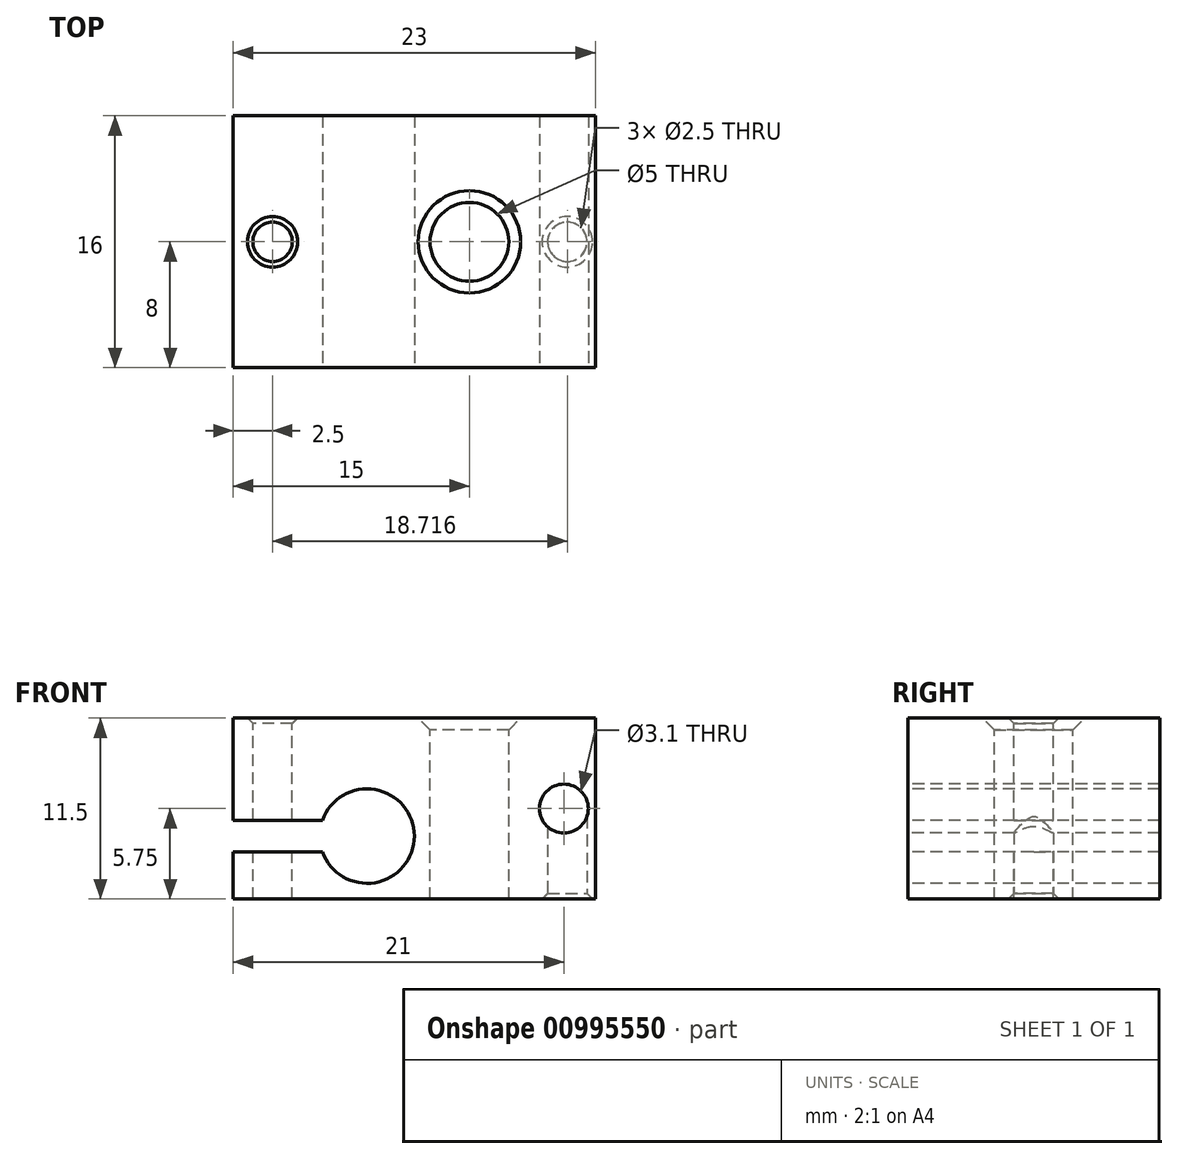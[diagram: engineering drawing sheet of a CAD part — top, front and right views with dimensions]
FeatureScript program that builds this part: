
annotation { "Feature Type Name" : "Feature", "Feature Type Description" : "" }
export const myFeature = defineFeature(function(context is Context, id is Id, definition is map)
    precondition{}
    {
        {
            var Q0;
            Q0=qCreatedBy(makeId("Top.planeOp"),FACE);
            var sketch = newSketch(context, id + "F0", { "sketchPlane" : qUnion([Q0])});
            skLineSegment(sketch, "E0.bottom", {"start": v(-11.5, 8) * mm, "end": v(11.5, 8) * mm});
            skLineSegment(sketch, "E0.top", {"start": v(-11.5, -8) * mm, "end": v(11.5, -8) * mm});
            skLineSegment(sketch, "E0.left", {"start": v(-11.5, 8) * mm, "end": v(-11.5, -8) * mm});
            skLineSegment(sketch, "E0.right", {"start": v(11.5, 8) * mm, "end": v(11.5, -8) * mm});
            skPoint(sketch, "E0.middle", {"position": v(0, 0) * mm});
            skSolve(sketch);
        }
        {
            var Q0;
            Q0=makeQuery(id+"F0.imprint","IMPRINT",FACE,{"disambiguationData":[TD([[makeQuery(id+"F0.imprint","IMPRINT",EDGE,{"derivedFrom":sQuery(id+"F0.wireOp",EDGE,"E0.bottom")}),-1.0]])]});
            extrude(context, id + "F1", {"entities" : qUnion([Q0]), "depth" : 11.5 * mm, "offsetDistance" : 25 * mm});
        }
        {
            var Q0;
            Q0=makeQuery(id+"F1.opExtrude","CAP_FACE",FACE,{"disambiguationData":[OSD([sQuery(id+"F0.wireOp",EDGE,"E0.bottom"),sQuery(id+"F0.wireOp",EDGE,"E0.top"),sQuery(id+"F0.wireOp",EDGE,"E0.left"),sQuery(id+"F0.wireOp",EDGE,"E0.right")])],"isStart":false});
            var sketch = newSketch(context, id + "F2", { "sketchPlane" : qUnion([Q0])});
            skPoint(sketch, "E1", {"position": v(3.5, 0) * mm});
            skPoint(sketch, "E2", {"position": v(-14.22, 0) * mm});
            skPoint(sketch, "E3", {"position": v(-9, 0) * mm});
            skSolve(sketch);
        }
        {
            var Q0;
            Q0=sQuery(id+"F2.wireOp",VERTEX,"E1");
            var Q1;
            Q1=makeQuery(id+"F1.opExtrude","SWEPT_BODY",BODY,{"disambiguationData":[OSD([sQuery(id+"F0.wireOp",EDGE,"E0.bottom"),sQuery(id+"F0.wireOp",EDGE,"E0.top"),sQuery(id+"F0.wireOp",EDGE,"E0.left"),sQuery(id+"F0.wireOp",EDGE,"E0.right")])]});
            hole(context, id + "F3", {"style" : HoleStyle.C_SINK, "endStyle" : HoleEndStyle.THROUGH, "holeDiameter" : 5 * mm, "cSinkDiameter" : 6.5 * mm, "cSinkAngle" : 90 * degree, "majorDiameter" : 6 * mm, "isTappedThrough" : true, "tappedDepth" : 12 * mm, "tapClearance" : 3, "locations" : qUnion([Q0]), "scope" : qUnion([Q1])});
        }
        {
            var Q0;
            Q0=sQuery(id+"F2.wireOp",VERTEX,"E3");
            var Q1;
            Q1=makeQuery(id+"F1.opExtrude","SWEPT_BODY",BODY,{"disambiguationData":[OSD([sQuery(id+"F0.wireOp",EDGE,"E0.bottom"),sQuery(id+"F0.wireOp",EDGE,"E0.top"),sQuery(id+"F0.wireOp",EDGE,"E0.left"),sQuery(id+"F0.wireOp",EDGE,"E0.right")])]});
            hole(context, id + "F4", {"style" : HoleStyle.C_SINK, "endStyle" : HoleEndStyle.THROUGH, "holeDiameter" : 2.5 * mm, "cSinkDiameter" : 3.2 * mm, "cSinkAngle" : 90 * degree, "majorDiameter" : 5 * mm, "isTappedThrough" : true, "tappedDepth" : 12 * mm, "tapClearance" : 3, "locations" : qUnion([Q0]), "scope" : qUnion([Q1])});
        }
        {
            var Q0;
            Q0=makeQuery(id+"F1.opExtrude","SWEPT_FACE",FACE,{"disambiguationData":[OSD([sQuery(id+"F0.wireOp",EDGE,"E0.top")])]});
            var sketch = newSketch(context, id + "F5", { "sketchPlane" : qUnion([Q0])});
            skPoint(sketch, "E4.positionSnap0", {"position": v(11.5, 5.75) * mm});
            skPoint(sketch, "E5", {"position": v(-3, 4) * mm});
            skCircle(sketch, "E6", {"center": v(9.5, 5.75) * mm, "radius": 1.55 * mm});
            skCircle(sketch, "E7", {"center": v(-3, 4) * mm, "radius": 3 * mm});
            skLineSegment(sketch, "E8", {"start": v(-12.25, 3) * mm, "end": v(-4.59, 3) * mm});
            skLineSegment(sketch, "E9", {"start": v(-4.59, 3) * mm, "end": v(-4.59, 5) * mm});
            skLineSegment(sketch, "E10", {"start": v(-4.59, 5) * mm, "end": v(-12.25, 5) * mm});
            skLineSegment(sketch, "E11", {"start": v(-12.25, 5) * mm, "end": v(-12.25, 3) * mm});
            skSolve(sketch);
        }
        {
            var Q0;
            Q0=makeQuery(id+"F5.imprint","IMPRINT",FACE,{"disambiguationData":[TD([[makeQuery(id+"F5.imprint","IMPRINT",EDGE,{"derivedFrom":sQuery(id+"F5.wireOp",EDGE,"E7")}),1.0]])]});
            var Q1;
            Q1=makeQuery(id+"F5.imprint","IMPRINT",FACE,{"disambiguationData":[TD([[makeQuery(id+"F5.imprint","IMPRINT",EDGE,{"derivedFrom":sQuery(id+"F5.wireOp",EDGE,"E6")}),1.0]])]});
            var Q2;
            {var subQ0=sQuery(id+"F5.wireOp",EDGE,"E8");var subQ1=sQuery(id+"F5.wireOp",EDGE,"E7");var subQ2=makeQuery(id+"F5.imprint","INTERSECT",VERTEX,{"derivedFrom":[subQ1,subQ0]});Q2=makeQuery(id+"F5.imprint","IMPRINT",FACE,{"disambiguationData":[TD([[makeQuery(id+"F5.imprint","IMPRINT",EDGE,{"disambiguationData":[TD([[subQ2,1.0]])],"derivedFrom":subQ1}),-1.0]])]});}
            extrude(context, id + "F6", {"entities" : qUnion([Q0, Q1, Q2]), "operationType" : NewBodyOperationType.REMOVE, "endBound" : BoundingType.THROUGH_ALL, "oppositeDirection" : true, "depth" : 25 * mm, "offsetDistance" : 25 * mm});
        }
        {
            var Q0;
            Q0=makeQuery(id+"F1.opExtrude","CAP_FACE",FACE,{"disambiguationData":[OSD([sQuery(id+"F0.wireOp",EDGE,"E0.bottom"),sQuery(id+"F0.wireOp",EDGE,"E0.top"),sQuery(id+"F0.wireOp",EDGE,"E0.left"),sQuery(id+"F0.wireOp",EDGE,"E0.right")])],"isStart":true});
            var sketch = newSketch(context, id + "F7", { "sketchPlane" : qUnion([Q0])});
            skPoint(sketch, "E12", {"position": v(9.72, 0) * mm});
            skSolve(sketch);
        }
        {
            var Q0;
            Q0=sQuery(id+"F7.wireOp",VERTEX,"E12");
            var Q1;
            Q1=makeQuery(id+"F1.opExtrude","SWEPT_BODY",BODY,{"disambiguationData":[OSD([sQuery(id+"F0.wireOp",EDGE,"E0.bottom"),sQuery(id+"F0.wireOp",EDGE,"E0.top"),sQuery(id+"F0.wireOp",EDGE,"E0.left"),sQuery(id+"F0.wireOp",EDGE,"E0.right")])]});
            hole(context, id + "F8", {"style" : HoleStyle.C_SINK, "endStyle" : HoleEndStyle.BLIND, "holeDiameter" : 2.5 * mm, "cSinkDiameter" : 3.2 * mm, "cSinkAngle" : 90 * degree, "majorDiameter" : 5 * mm, "holeDepth" : (11.5 / 2) * mm, "isTappedThrough" : true, "tappedDepth" : 12 * mm, "tapClearance" : 3, "locations" : qUnion([Q0]), "scope" : qUnion([Q1])});
        }
    });
